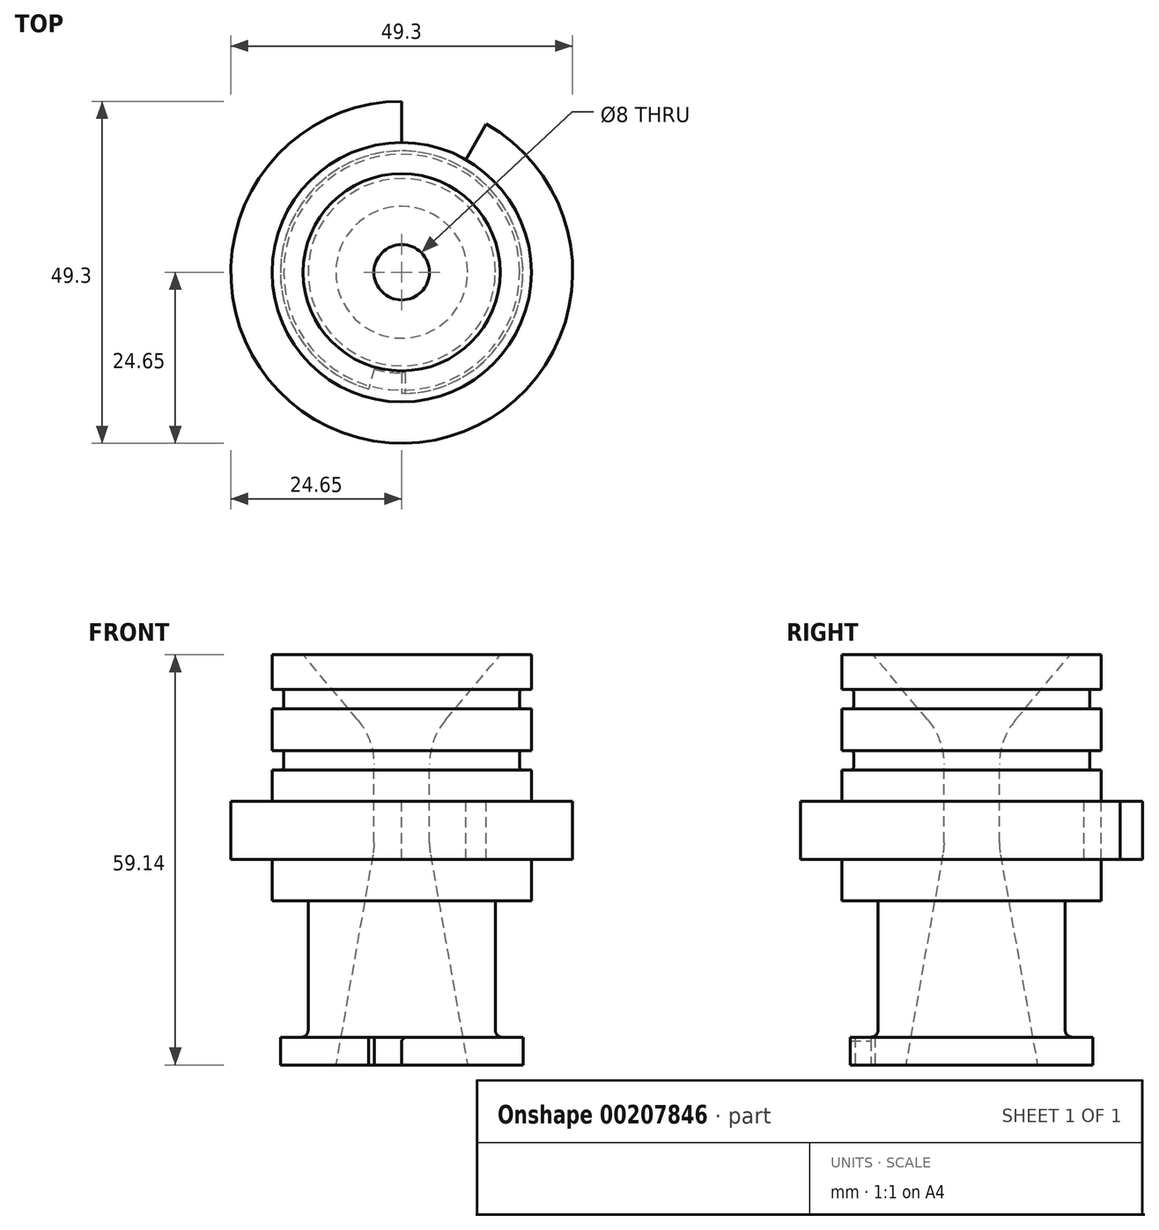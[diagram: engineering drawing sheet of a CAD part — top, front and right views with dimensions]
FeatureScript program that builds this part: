
annotation { "Feature Type Name" : "Feature", "Feature Type Description" : "" }
export const myFeature = defineFeature(function(context is Context, id is Id, definition is map)
    precondition{}
    {
        {
            var Q0;
            Q0=qCreatedBy(makeId("Front.planeOp"),FACE);
            var sketch = newSketch(context, id + "F0", { "sketchPlane" : qUnion([Q0])});
            skLineSegment(sketch, "E0", {"start": v(-18.7, 0) * mm, "end": v(-18.7, 6) * mm});
            skLineSegment(sketch, "E1", {"start": v(-18.7, 6) * mm, "end": v(-24.65, 6) * mm});
            skLineSegment(sketch, "E2", {"start": v(-24.65, 6) * mm, "end": v(-24.65, 14.4) * mm});
            skLineSegment(sketch, "E3", {"start": v(-18.7, 14.4) * mm, "end": v(-18.7, 18.9) * mm});
            skLineSegment(sketch, "E4", {"start": v(-18.7, 18.9) * mm, "end": v(-17.42, 18.9) * mm});
            skLineSegment(sketch, "E5", {"start": v(-17.02, 19.3) * mm, "end": v(-17.02, 21.3) * mm});
            skLineSegment(sketch, "E6", {"start": v(-17.42, 21.7) * mm, "end": v(-18.7, 21.7) * mm});
            skLineSegment(sketch, "E7", {"start": v(-18.7, 21.7) * mm, "end": v(-18.7, 27.7) * mm});
            skLineSegment(sketch, "E8", {"start": v(-18.7, 27.7) * mm, "end": v(-17.42, 27.7) * mm});
            skLineSegment(sketch, "E9", {"start": v(-17.02, 28.1) * mm, "end": v(-17.02, 30.1) * mm});
            skLineSegment(sketch, "E10", {"start": v(-17.42, 30.5) * mm, "end": v(-18.7, 30.5) * mm});
            skLineSegment(sketch, "E11", {"start": v(-18.7, 14.4) * mm, "end": v(-24.65, 14.4) * mm});
            skLineSegment(sketch, "E12", {"start": v(-14.22, 35.5) * mm, "end": v(-6.34, 26.11) * mm});
            skLineSegment(sketch, "E13", {"start": v(-4, 8.43) * mm, "end": v(-4, 19.68) * mm});
            skLineSegment(sketch, "E14", {"start": v(0, 48.19) * mm, "end": v(0, -42.57) * mm});
            skPoint(sketch, "E15.visualSharp", {"position": v(-4, 23.32) * mm});
            skArc(sketch, "E15.filletArc", {"start": v(-4, 19.68) * mm, "mid": v(-4.6, 23.1) * mm, "end": v(-6.34, 26.11) * mm});
            skPoint(sketch, "E16.visualSharp", {"position": v(-4, 7.32) * mm});
            skArc(sketch, "E16.filletArc", {"start": v(-4.15, 6.7) * mm, "mid": v(-4.04, 7.55) * mm, "end": v(-4, 8.43) * mm});
            skLineSegment(sketch, "E17", {"start": v(-18.7, 30.5) * mm, "end": v(-18.7, 35.5) * mm});
            skLineSegment(sketch, "E18", {"start": v(-18.7, 35.5) * mm, "end": v(-14.22, 35.5) * mm});
            skLineSegment(sketch, "E19", {"start": v(-4.15, 6.7) * mm, "end": v(-9.5, -23.64) * mm});
            skLineSegment(sketch, "E20", {"start": v(-13.5, 0) * mm, "end": v(-18.7, 0) * mm});
            skLineSegment(sketch, "E21", {"start": v(-17.5, -23.64) * mm, "end": v(-17.5, -19.64) * mm});
            skLineSegment(sketch, "E22", {"start": v(-17.5, -19.64) * mm, "end": v(-14.5, -19.64) * mm});
            skLineSegment(sketch, "E23", {"start": v(-13.5, -18.64) * mm, "end": v(-13.5, 0) * mm});
            skLineSegment(sketch, "E24", {"start": v(-17.5, -23.64) * mm, "end": v(-9.5, -23.64) * mm});
            skPoint(sketch, "E25.visualSharp", {"position": v(-13.5, -19.64) * mm});
            skArc(sketch, "E25.filletArc", {"start": v(-14.5, -19.64) * mm, "mid": v(-13.8, -19.35) * mm, "end": v(-13.5, -18.64) * mm});
            skPoint(sketch, "E26.visualSharp", {"position": v(-17.02, 30.5) * mm});
            skArc(sketch, "E26.filletArc", {"start": v(-17.02, 30.1) * mm, "mid": v(-17.14, 30.38) * mm, "end": v(-17.42, 30.5) * mm});
            skPoint(sketch, "E27.visualSharp", {"position": v(-17.02, 27.7) * mm});
            skArc(sketch, "E27.filletArc", {"start": v(-17.42, 27.7) * mm, "mid": v(-17.14, 27.82) * mm, "end": v(-17.02, 28.1) * mm});
            skPoint(sketch, "E28.visualSharp", {"position": v(-17.02, 21.7) * mm});
            skArc(sketch, "E28.filletArc", {"start": v(-17.02, 21.3) * mm, "mid": v(-17.14, 21.58) * mm, "end": v(-17.42, 21.7) * mm});
            skPoint(sketch, "E29.visualSharp", {"position": v(-17.02, 18.9) * mm});
            skArc(sketch, "E29.filletArc", {"start": v(-17.42, 18.9) * mm, "mid": v(-17.14, 19.02) * mm, "end": v(-17.02, 19.3) * mm});
            skSolve(sketch);
        }
        {
            var Q0;
            Q0=qSketchRegion(id+"F0",true);
            var Q1;
            Q1=sQuery(id+"F0.wireOp",EDGE,"E14");
            revolve(context, id + "F1", {"entities" : qUnion([Q0]), "axis" : qUnion([Q1]), "revolveType" : RevolveType.FULL});
        }
        {
            var Q0;
            Q0=makeQuery(id+"F1.opRevolve","SWEPT_FACE",FACE,{"disambiguationData":[OSD([sQuery(id+"F0.wireOp",EDGE,"E11")])]});
            var sketch = newSketch(context, id + "F2", { "sketchPlane" : qUnion([Q0])});
            skCircle(sketch, "E30.cCircle", {"center": v(0, 0) * mm, "radius": 18.7 * mm, "construction": true});
            skLineSegment(sketch, "E30.0", {"start": v(9.35, -16.2) * mm, "end": v(-9.35, -16.2) * mm});
            skLineSegment(sketch, "E30.1", {"start": v(-9.35, -16.2) * mm, "end": v(-18.7, 0) * mm});
            skLineSegment(sketch, "E30.2", {"start": v(-18.7, 0) * mm, "end": v(-9.35, 16.2) * mm});
            skLineSegment(sketch, "E30.3", {"start": v(-9.35, 16.2) * mm, "end": v(9.35, 16.2) * mm});
            skLineSegment(sketch, "E30.4", {"start": v(9.35, 16.2) * mm, "end": v(18.7, 0) * mm});
            skLineSegment(sketch, "E30.5", {"start": v(18.7, 0) * mm, "end": v(9.35, -16.2) * mm});
            skLineSegment(sketch, "E31.0", {"start": v(0, -18.7) * mm, "end": v(-16.2, -9.35) * mm});
            skLineSegment(sketch, "E31.1", {"start": v(-16.2, -9.35) * mm, "end": v(-16.2, 9.35) * mm});
            skLineSegment(sketch, "E31.2", {"start": v(-16.2, 9.35) * mm, "end": v(0, 18.7) * mm});
            skLineSegment(sketch, "E31.3", {"start": v(0, 18.7) * mm, "end": v(16.2, 9.35) * mm});
            skLineSegment(sketch, "E31.4", {"start": v(16.2, 9.35) * mm, "end": v(16.2, -9.35) * mm});
            skLineSegment(sketch, "E31.5", {"start": v(16.2, -9.35) * mm, "end": v(0, -18.7) * mm});
            skLineSegment(sketch, "E32", {"start": v(0, 18.7) * mm, "end": v(0, 24.65) * mm});
            skLineSegment(sketch, "E33", {"start": v(9.26, 16.24) * mm, "end": v(12.21, 21.41) * mm});
            skSolve(sketch);
        }
        {
            var Q0;
            {var subQ0=sQuery(id+"F2.wireOp",EDGE,"E32");Q0=makeQuery(id+"F2.imprint","IMPRINT",FACE,{"disambiguationData":[TD([[makeQuery(id+"F2.imprint","IMPRINT",EDGE,{"derivedFrom":subQ0}),-1.0]])]});}
            extrude(context, id + "F3", {"entities" : qUnion([Q0]), "operationType" : NewBodyOperationType.REMOVE, "endBound" : BoundingType.THROUGH_ALL, "oppositeDirection" : true, "depth" : 25 * mm});
        }
        {
            var Q0;
            Q0=makeQuery(id+"F1.opRevolve","SWEPT_FACE",FACE,{"disambiguationData":[OSD([sQuery(id+"F0.wireOp",EDGE,"E24")])]});
            var sketch = newSketch(context, id + "F4", { "sketchPlane" : qUnion([Q0])});
            skCircle(sketch, "E34", {"center": v(0, 0) * mm, "radius": 14.5 * mm});
            skLineSegment(sketch, "E35", {"start": v(0, 14.5) * mm, "end": v(0, 17.5) * mm});
            skPoint(sketch, "E36", {"position": v(-3.96, 13.95) * mm});
            skLineSegment(sketch, "E37", {"start": v(-3.96, 13.95) * mm, "end": v(-4.78, 16.83) * mm});
            skSolve(sketch);
        }
        {
            var Q0;
            {var subQ0=sQuery(id+"F4.wireOp",EDGE,"E35");Q0=makeQuery(id+"F4.imprint","IMPRINT",FACE,{"disambiguationData":[TD([[makeQuery(id+"F4.imprint","IMPRINT",EDGE,{"derivedFrom":subQ0}),1.0]])]});}
            extrude(context, id + "F5", {"entities" : qUnion([Q0]), "operationType" : NewBodyOperationType.REMOVE, "oppositeDirection" : true, "depth" : 10 * mm});
        }
        {
            var Q0;
            Q0=makeQuery(id+"F5.boolean.opBoolean","INTERSECT",EDGE,{"derivedFrom":[makeQuery(id+"F1.opRevolve","SWEPT_FACE",FACE,{"disambiguationData":[OSD([sQuery(id+"F0.wireOp",EDGE,"E22")])]}),makeQuery(id+"F5.opExtrude","SWEPT_FACE",FACE,{"disambiguationData":[OSD([sQuery(id+"F4.wireOp",EDGE,"E35")])]})]});
            var Q1;
            Q1=makeQuery(id+"FkxyIgEDrVSvux5_1.1.F5.boolean.opBoolean","INTERSECT",EDGE,{"derivedFrom":[makeQuery(id+"F1.opRevolve","SWEPT_FACE",FACE,{"disambiguationData":[OSD([sQuery(id+"F0.wireOp",EDGE,"E22")])]}),makeQuery(id+"FkxyIgEDrVSvux5_1.1.F5.opExtrude","SWEPT_FACE",FACE,{"disambiguationData":[OSD([sQuery(id+"F4.wireOp",EDGE,"E35")])]})]});
            var Q2;
            {var subQ0=sQuery(id+"F4.wireOp",EDGE,"E35");Q2=makeQuery(id+"FkxyIgEDrVSvux5_1.2.F5.boolean.opBoolean","INTERSECT",EDGE,{"derivedFrom":[makeQuery(id+"FkxyIgEDrVSvux5_1.1.F5.boolean.opBoolean","SPLIT",FACE,{"disambiguationData":[TD([makeQuery(id+"F5.boolean.opBoolean","COPY",FACE,{"derivedFrom":makeQuery(id+"F5.opExtrude","SWEPT_FACE",FACE,{"disambiguationData":[OSD([sQuery(id+"F4.wireOp",EDGE,"E37")])]})})])],"derivedFrom":makeQuery(id+"F1.opRevolve","SWEPT_FACE",FACE,{"disambiguationData":[OSD([sQuery(id+"F0.wireOp",EDGE,"E22")])]})}),makeQuery(id+"FkxyIgEDrVSvux5_1.2.F5.opExtrude","SWEPT_FACE",FACE,{"disambiguationData":[OSD([subQ0])]})]});}
            var Q3;
            {var subQ0=sQuery(id+"F4.wireOp",EDGE,"E35");var subQ1=makeQuery(id+"F5.boolean.opBoolean","COPY",FACE,{"derivedFrom":makeQuery(id+"F5.opExtrude","SWEPT_FACE",FACE,{"disambiguationData":[OSD([sQuery(id+"F4.wireOp",EDGE,"E37")])]})});var subQ2=sQuery(id+"F4.wireOp",EDGE,"E34");var subQ3=makeQuery(id+"F5.boolean.opBoolean","COPY",FACE,{"derivedFrom":makeQuery(id+"F5.opExtrude","SWEPT_FACE",FACE,{"disambiguationData":[OSD([subQ2])]})});Q3=makeQuery(id+"FkxyIgEDrVSvux5_1.3.F5.boolean.opBoolean","INTERSECT",EDGE,{"derivedFrom":[makeQuery(id+"FkxyIgEDrVSvux5_1.2.F5.boolean.opBoolean","SPLIT",FACE,{"disambiguationData":[TD([subQ3])],"derivedFrom":makeQuery(id+"FkxyIgEDrVSvux5_1.1.F5.boolean.opBoolean","SPLIT",FACE,{"disambiguationData":[TD([subQ1])],"derivedFrom":makeQuery(id+"F1.opRevolve","SWEPT_FACE",FACE,{"disambiguationData":[OSD([sQuery(id+"F0.wireOp",EDGE,"E22")])]})})}),makeQuery(id+"FkxyIgEDrVSvux5_1.3.F5.opExtrude","SWEPT_FACE",FACE,{"disambiguationData":[OSD([subQ0])]})]});}
            chamfer(context, id + "F6", {"entities" : qUnion([Q0, Q1, Q2, Q3]), "width" : .5 * mm, "tangentPropagation" : true});
        }
    });
